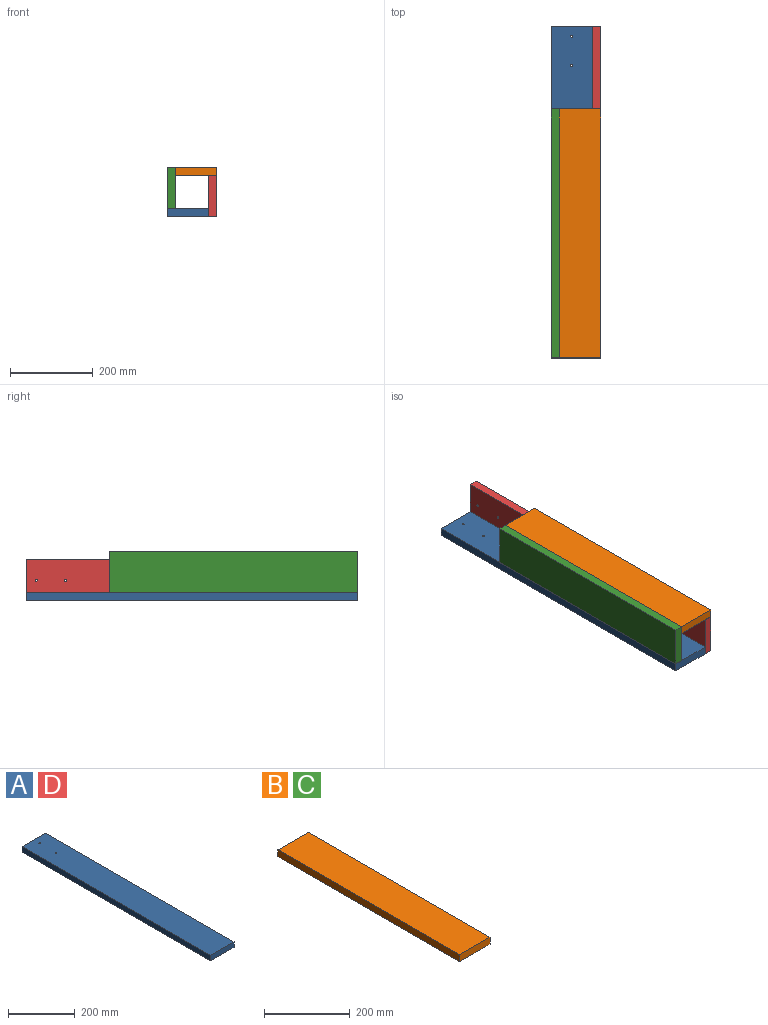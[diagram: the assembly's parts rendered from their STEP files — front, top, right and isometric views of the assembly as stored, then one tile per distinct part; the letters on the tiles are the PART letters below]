
ASSEMBLY  parts=4 mates=10
PART A: 8 faces, bbox 100x800x20 mm
  f0: plane 800x20mm, normal (-1,0,0), area 16000mm2, adj f2,f3,f4,f7
  f1: plane 800x20mm, normal (1,0,0), area 16000mm2, adj f2,f3,f4,f7
  f2: plane 100x20mm, normal (0,1,0), area 2000mm2, adj f0,f1,f3,f4
  f3: plane 800x100mm, normal (0,0,1), area 79960.7mm2, adj f0,f1,f2,f5,f6,f7
  f4: plane 800x100mm, normal (0,0,-1), area 79960.7mm2, adj f0,f1,f2,f5,f6,f7
  f5: cylinder r=2.5mm len=20mm, axis (0,0,1), area 314.2mm2, adj f3,f4
  f6: cylinder r=2.5mm len=20mm, axis (0,0,1), area 314.2mm2, adj f3,f4
  f7: plane 100x20mm, normal (0,-1,0), area 2000mm2, adj f0,f1,f3,f4
PART B: 6 faces, bbox 100x600x20 mm
  f0: plane 600x20mm, normal (-1,0,0), area 12000mm2, adj f2,f3,f4,f5
  f1: plane 600x20mm, normal (1,0,0), area 12000mm2, adj f2,f3,f4,f5
  f2: plane 600x100mm, normal (0,0,1), area 60000mm2, adj f0,f1,f4,f5
  f3: plane 600x100mm, normal (0,0,-1), area 60000mm2, adj f0,f1,f4,f5
  f4: plane 100x20mm, normal (0,1,0), area 2000mm2, adj f0,f1,f2,f3
  f5: plane 100x20mm, normal (0,-1,0), area 2000mm2, adj f0,f1,f2,f3
PART C: same geometry as B
PART D: same geometry as A
PLACE A t=(489.81,-357.85,179.11)mm
PLACE B t=(509.81,-357.85,279.11)mm
PLACE C rot(axis=(0,-1,0),90deg) t=(509.81,-357.85,199.11)mm
PLACE D rot(axis=(0,-1,0),90deg) t=(609.81,-357.85,179.11)mm
MATE parallel A.f2 <-> D.f2  axis (0,1,0) through (489.81,642.15,199.11)mm
MATE parallel A.f4 <-> D.f0  axis (0,0,-1) through (539.81,241.98,179.11)mm
MATE planar A.f1 <-> D.f3  axis (1,0,0) through (589.81,242.15,189.11)mm
MATE parallel A.f3 <-> D.f1  axis (0,0,1) through (489.81,242.15,199.11)mm
MATE parallel A.f4 <-> D.f0  axis (0,0,-1) through (539.81,241.98,179.11)mm
MATE parallel C.f2 <-> A.f0  axis (-1,0,0) through (489.81,142.15,249.11)mm
MATE parallel A.f4 <-> D.f0  axis (0,0,-1) through (539.81,241.98,179.11)mm
MATE planar C.f3 <-> B.f0  axis (1,0,0) through (509.81,142.15,249.11)mm
MATE planar A.f3 <-> C.f0  axis (0,0,1) through (539.81,241.98,199.11)mm
MATE parallel C.f4 <-> A.f2  axis (0,1,0) through (499.81,442.15,249.11)mm
